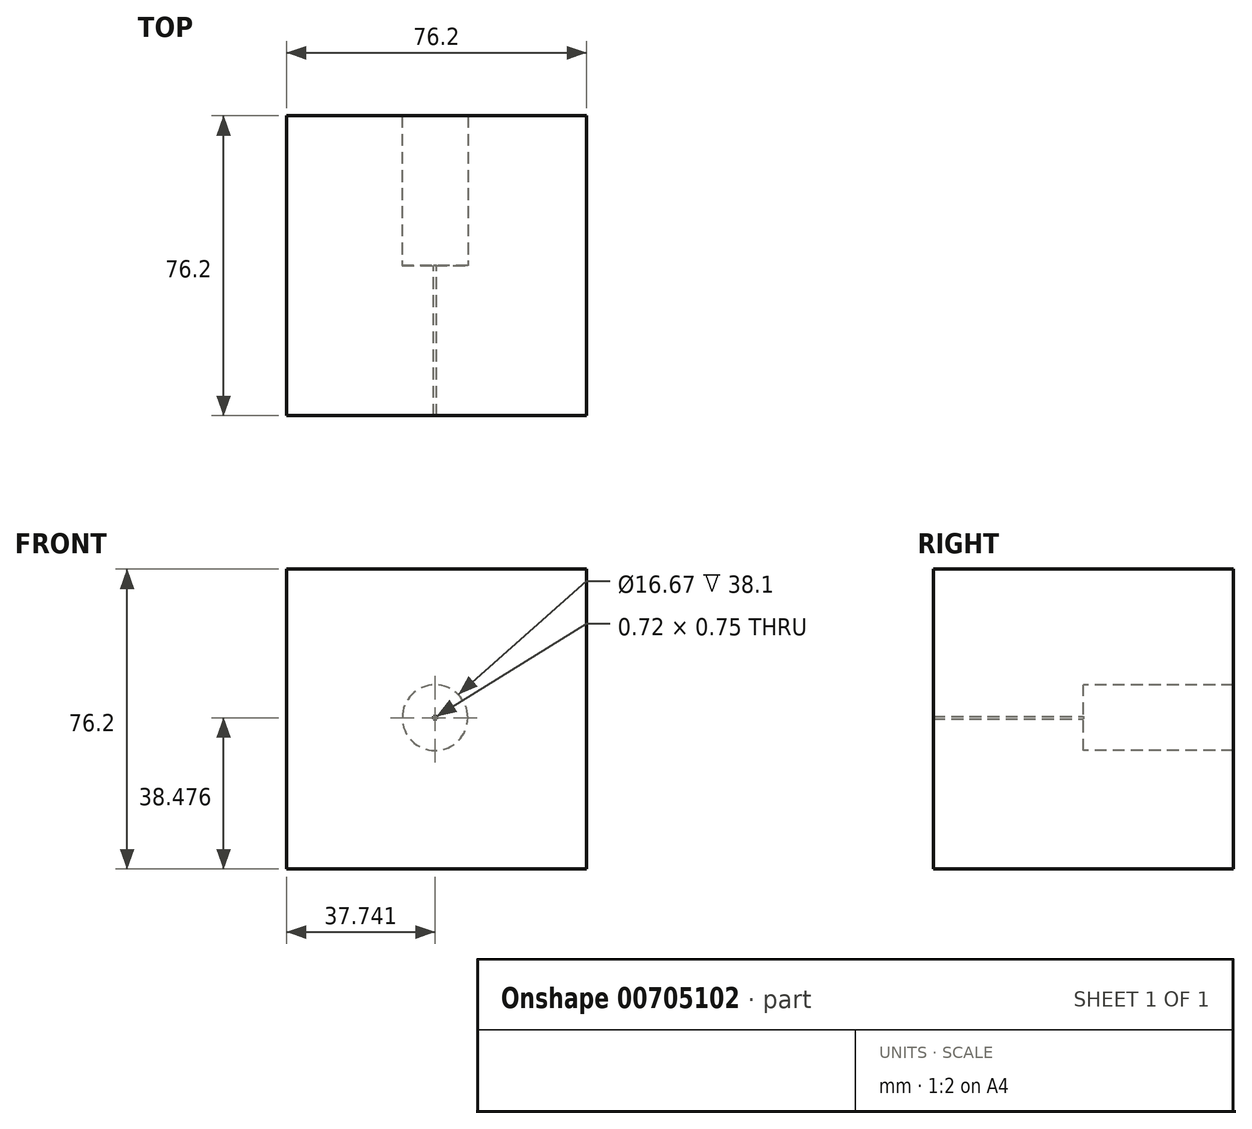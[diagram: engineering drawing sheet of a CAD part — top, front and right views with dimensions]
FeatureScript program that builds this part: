
annotation { "Feature Type Name" : "Feature", "Feature Type Description" : "" }
export const myFeature = defineFeature(function(context is Context, id is Id, definition is map)
    precondition{}
    {
        {
            var Q0;
            Q0=qCreatedBy(makeId("Front.planeOp"),FACE);
            var sketch = newSketch(context, id + "F0", { "sketchPlane" : qUnion([Q0])});
            skLineSegment(sketch, "E0.bottom", {"start": v(-2.1, 8.31) * mm, "end": v(-1.39, 8.31) * mm});
            skLineSegment(sketch, "E0.top", {"start": v(-2.1, 9.06) * mm, "end": v(-1.39, 9.06) * mm});
            skLineSegment(sketch, "E0.left", {"start": v(-2.1, 8.31) * mm, "end": v(-2.1, 9.06) * mm});
            skLineSegment(sketch, "E0.right", {"start": v(-1.39, 8.31) * mm, "end": v(-1.39, 9.06) * mm});
            skPoint(sketch, "E0.middle", {"position": v(-1.75, 8.69) * mm});
            skCircle(sketch, "E1", {"center": v(-1.75, 8.43) * mm, "radius": 0.01 * mm});
            skCircle(sketch, "E2", {"center": v(-1.74, 8.43) * mm, "radius": 0.01 * mm});
            skCircle(sketch, "E3", {"center": v(-1.73, 8.43) * mm, "radius": 0.01 * mm});
            skLineSegment(sketch, "E4.bottom", {"start": v(36.71, 46.41) * mm, "end": v(-39.49, 46.41) * mm});
            skLineSegment(sketch, "E4.top", {"start": v(36.71, -29.79) * mm, "end": v(-39.49, -29.79) * mm});
            skLineSegment(sketch, "E4.left", {"start": v(36.71, 46.41) * mm, "end": v(36.71, -29.79) * mm});
            skLineSegment(sketch, "E4.right", {"start": v(-39.49, 46.41) * mm, "end": v(-39.49, -29.79) * mm});
            skPoint(sketch, "E4.middle", {"position": v(-1.39, 8.31) * mm});
            skSolve(sketch);
        }
        {
            var Q0;
            Q0=makeQuery(id+"F0.imprint","IMPRINT",FACE,{"disambiguationData":[TD([[makeQuery(id+"F0.imprint","IMPRINT",EDGE,{"derivedFrom":sQuery(id+"F0.wireOp",EDGE,"E0.bottom")}),-1.0]])]});
            extrude(context, id + "F1", {"entities" : qUnion([Q0]), "endBound" : BoundingType.SYMMETRIC, "depth" : 76.2 * mm, "offsetDistance" : 25.4 * mm});
        }
        {
            var Q0;
            Q0=sQuery(id+"F0.wireOp",VERTEX,"E0.middle");
            var Q1;
            Q1=makeQuery(id+"F1.opExtrude","SWEPT_BODY",BODY,{"disambiguationData":[OSD([sQuery(id+"F0.wireOp",EDGE,"E0.bottom"),sQuery(id+"F0.wireOp",EDGE,"E0.top"),sQuery(id+"F0.wireOp",EDGE,"E0.left"),sQuery(id+"F0.wireOp",EDGE,"E0.right"),sQuery(id+"F0.wireOp",EDGE,"E4.bottom"),sQuery(id+"F0.wireOp",EDGE,"E4.top"),sQuery(id+"F0.wireOp",EDGE,"E4.left"),sQuery(id+"F0.wireOp",EDGE,"E4.right")])]});
            hole(context, id + "F2", {"style" : HoleStyle.SIMPLE, "endStyle" : HoleEndStyle.BLIND, "standardTappedOrClearance" : lookupTablePath({ "standard" : "ANSI", "engagement" : "75%", "pitch" : "10 tpi", "size" : "3/4", "type" : "Tapped" }), "standardBlindInLast" : lookupTablePath({ "standard" : "ANSI", "engagement" : "75%", "pitch" : "10 tpi", "size" : "3/4", "type" : "Tapped" }), "holeDiameter" : 16.67 * mm, "majorDiameter" : 19.05 * mm, "showTappedDepth" : true, "holeDepth" : 58.42 * mm, "tappedDepth" : 50.8 * mm, "tapClearance" : 3, "locations" : qUnion([Q0]), "scope" : qUnion([Q1])});
        }
    });
